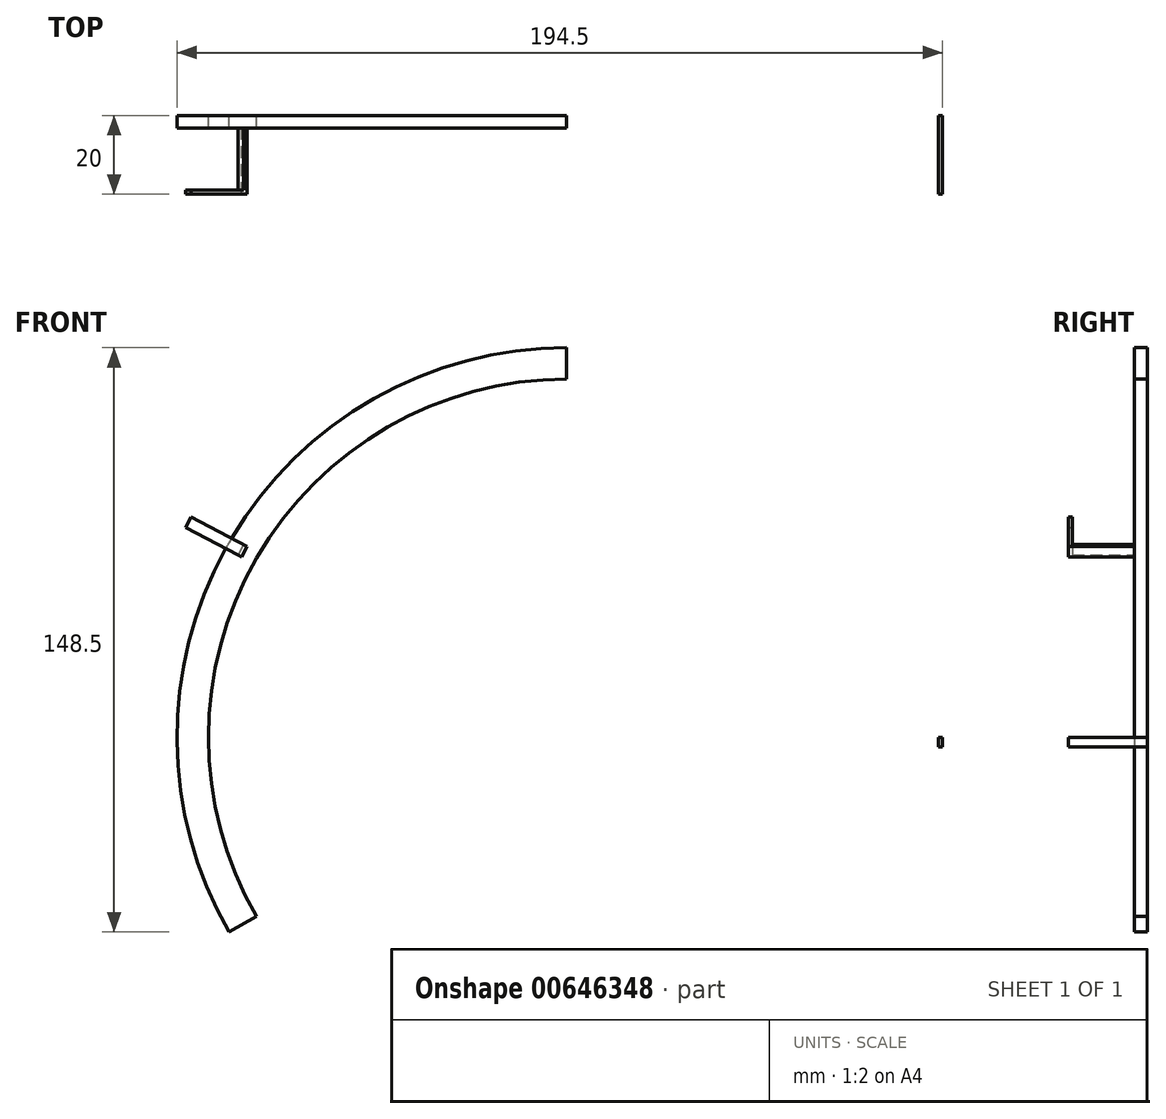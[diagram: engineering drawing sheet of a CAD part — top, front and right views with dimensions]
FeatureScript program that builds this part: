
annotation { "Feature Type Name" : "Feature", "Feature Type Description" : "" }
export const myFeature = defineFeature(function(context is Context, id is Id, definition is map)
    precondition{}
    {
        {
            var Q0;
            Q0=qCreatedBy(makeId("Front.planeOp"),FACE);
            var sketch = newSketch(context, id + "F0", { "sketchPlane" : qUnion([Q0])});
            skArc(sketch, "E0", {"start": v(0, 91) * mm, "mid": v(-78.8, 45.5) * mm, "end": v(-78.8, -45.5) * mm});
            skArc(sketch, "E1", {"start": v(0, 99) * mm, "mid": v(-85.74, 49.5) * mm, "end": v(-85.74, -49.5) * mm});
            skLineSegment(sketch, "E2", {"start": v(0, 91) * mm, "end": v(0, 99) * mm});
            skLineSegment(sketch, "E3.1.0", {"start": v(-78.8, -45.5) * mm, "end": v(-85.74, -49.5) * mm});
            skSolve(sketch);
        }
        {
            var Q0;
            Q0 = qSketchRegion(id + "F0", true);
            extrude(context, id + "F1", {"entities" : qUnion([Q0]), "depth" : 3.2 * mm, "offsetDistance" : 25 * mm});
        }
        {
            var Q0;
            Q0=qCreatedBy(makeId("Front.planeOp"),FACE);
            var sketch = newSketch(context, id + "F2", { "sketchPlane" : qUnion([Q0])});
            skLineSegment(sketch, "E4.bottom", {"start": v(95.5, 0) * mm, "end": v(94.5, 0) * mm});
            skLineSegment(sketch, "E4.top", {"start": v(95.5, -2.5) * mm, "end": v(94.5, -2.5) * mm});
            skLineSegment(sketch, "E4.left", {"start": v(95.5, 0) * mm, "end": v(95.5, -2.5) * mm});
            skLineSegment(sketch, "E4.right", {"start": v(94.5, 0) * mm, "end": v(94.5, -2.5) * mm});
            skPoint(sketch, "E5.center", {"position": v(0, 0) * mm});
            skLineSegment(sketch, "E6", {"start": v(-82.64, 45.84) * mm, "end": v(-83.52, 46.3) * mm});
            skLineSegment(sketch, "E7", {"start": v(-82.12, 48.95) * mm, "end": v(-81.23, 48.48) * mm});
            skLineSegment(sketch, "E8", {"start": v(-83.52, 46.3) * mm, "end": v(-82.12, 48.95) * mm});
            skLineSegment(sketch, "E9", {"start": v(-82.64, 45.84) * mm, "end": v(-81.23, 48.48) * mm});
            skLineSegment(sketch, "E10", {"start": v(-83.08, 46.07) * mm, "end": v(-82.64, 45.84) * mm});
            skPoint(sketch, "E11.orphan", {"position": v(-85.12, 50.55) * mm});
            skPoint(sketch, "E12.orphan", {"position": v(-86.62, 47.95) * mm});
            skPoint(sketch, "E13.orphan", {"position": v(-79.55, 44.2) * mm});
            skPoint(sketch, "E14.orphan", {"position": v(-78.05, 46.8) * mm});
            skSolve(sketch);
        }
        {
            var Q0;
            Q0 = qSketchRegion(id + "F2", true);
            extrude(context, id + "F3", {"entities" : qUnion([Q0]), "operationType" : NewBodyOperationType.ADD, "depth" : 20 * mm, "offsetDistance" : 25 * mm});
        }
        {
            var Q0;
            Q0=makeQuery(id+"F3.opExtrude","SWEPT_FACE",FACE,{"disambiguationData":[OSD([sQuery(id+"F2.wireOp",EDGE,"E8")])]});
            var sketch = newSketch(context, id + "F4", { "sketchPlane" : qUnion([Q0])});
            skLineSegment(sketch, "E15", {"start": v(19, 4.74) * mm, "end": v(19, 1.74) * mm});
            skSolve(sketch);
        }
        {
            var Q0;
            {var subQ0=sQuery(id+"F4.wireOp",EDGE,"E15");Q0=makeQuery(id+"F4.imprint","IMPRINT",FACE,{"disambiguationData":[TD([[makeQuery(id+"F4.imprint","IMPRINT",EDGE,{"derivedFrom":subQ0}),1.0]])]});}
            extrude(context, id + "F5", {"entities" : qUnion([Q0]), "operationType" : NewBodyOperationType.ADD, "depth" : 15 * mm, "offsetDistance" : 25 * mm});
        }
    });
